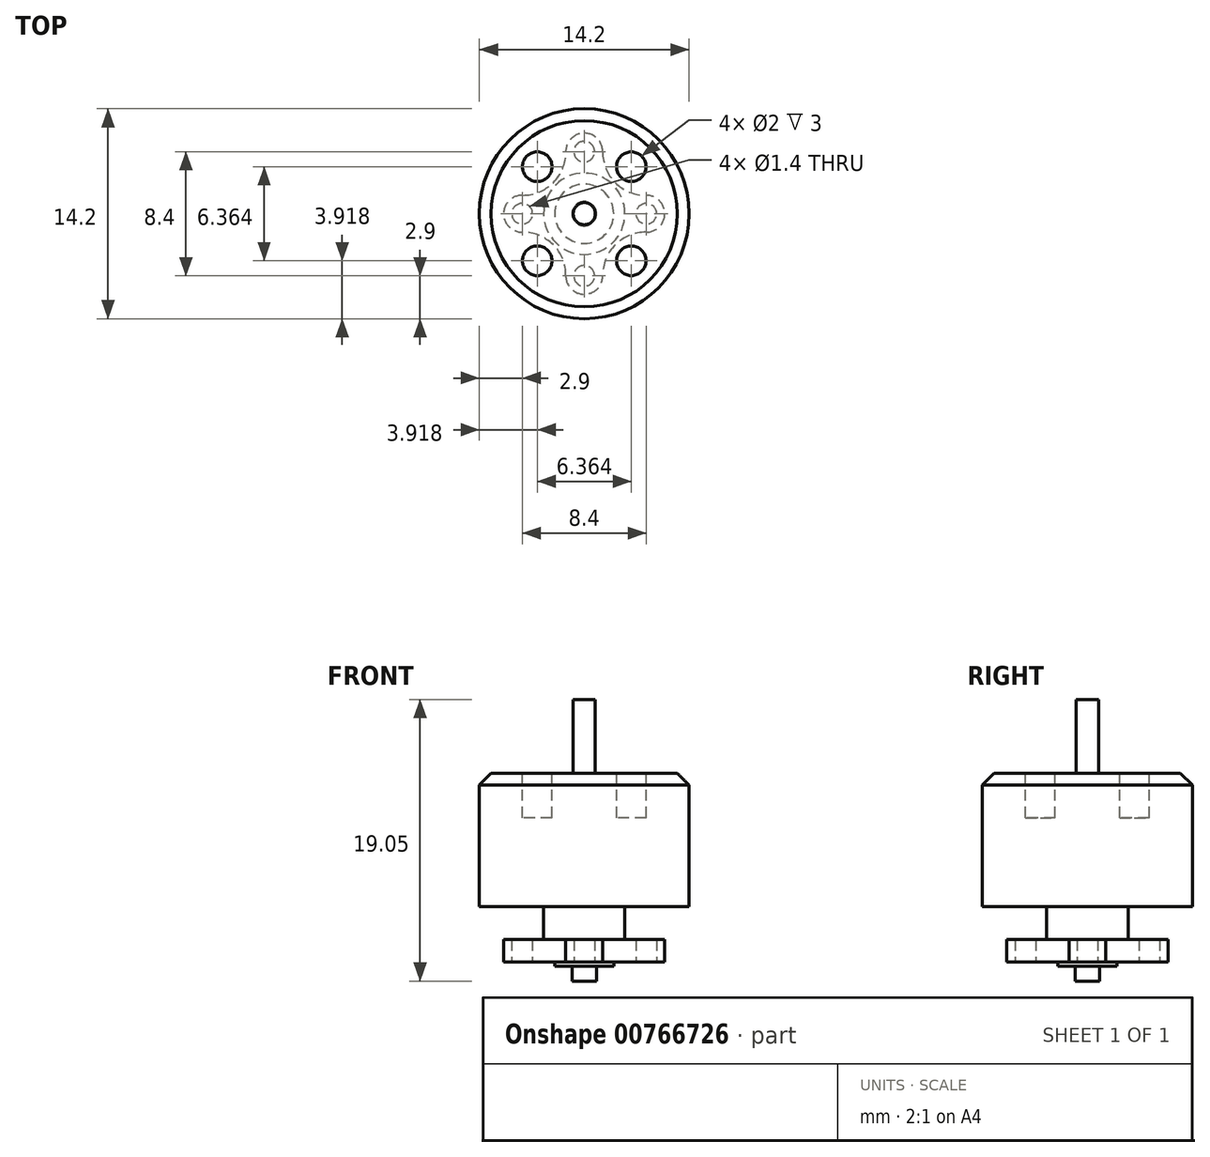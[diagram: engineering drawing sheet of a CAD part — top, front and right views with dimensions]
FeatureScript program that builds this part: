
annotation { "Feature Type Name" : "Feature", "Feature Type Description" : "" }
export const myFeature = defineFeature(function(context is Context, id is Id, definition is map)
    precondition{}
    {
        {
            var Q0;
            Q0=qCreatedBy(makeId("Top.planeOp"),FACE);
            var sketch = newSketch(context, id + "F0", { "sketchPlane" : qUnion([Q0])});
            skCircle(sketch, "E0", {"center": v(0, 0) * mm, "radius": 7.1 * mm});
            skSolve(sketch);
        }
        {
            var Q0;
            Q0 = qSketchRegion(id + "F0", true);
            extrude(context, id + "F1", {"entities" : qUnion([Q0]), "depth" : 9 * mm, "offsetDistance" : 25 * mm});
        }
        {
            var Q0;
            Q0=makeQuery(id+"F1.opExtrude","CAP_FACE",FACE,{"disambiguationData":[OSD([sQuery(id+"F0.wireOp",EDGE,"E0")])],"isStart":false});
            var sketch = newSketch(context, id + "F2", { "sketchPlane" : qUnion([Q0])});
            skCircle(sketch, "E1", {"center": v(0, 0) * mm, "radius": 0.75 * mm});
            skSolve(sketch);
        }
        {
            var Q0;
            Q0 = qSketchRegion(id + "F2", true);
            extrude(context, id + "F3", {"entities" : qUnion([Q0]), "operationType" : NewBodyOperationType.ADD, "depth" : 5 * mm, "offsetDistance" : 25 * mm});
        }
        {
            var Q0;
            Q0=makeQuery(id+"F1.opExtrude","CAP_FACE",FACE,{"disambiguationData":[OSD([sQuery(id+"F0.wireOp",EDGE,"E0")])],"isStart":false});
            var sketch = newSketch(context, id + "F4", { "sketchPlane" : qUnion([Q0])});
            skLineSegment(sketch, "E2.bottom", {"start": v(3.18, 3.18) * mm, "end": v(-3.18, 3.18) * mm, "construction": true});
            skLineSegment(sketch, "E2.top", {"start": v(3.18, -3.18) * mm, "end": v(-3.18, -3.18) * mm, "construction": true});
            skLineSegment(sketch, "E2.left", {"start": v(3.18, 3.18) * mm, "end": v(3.18, -3.18) * mm, "construction": true});
            skLineSegment(sketch, "E2.right", {"start": v(-3.18, 3.18) * mm, "end": v(-3.18, -3.18) * mm, "construction": true});
            skPoint(sketch, "E2.middle", {"position": v(0, 0) * mm});
            skCircle(sketch, "E3", {"center": v(3.18, 3.18) * mm, "radius": 1 * mm});
            skCircle(sketch, "E4", {"center": v(-3.18, 3.18) * mm, "radius": 1 * mm});
            skCircle(sketch, "E5", {"center": v(-3.18, -3.18) * mm, "radius": 1 * mm});
            skCircle(sketch, "E6", {"center": v(3.18, -3.18) * mm, "radius": 1 * mm});
            skSolve(sketch);
        }
        {
            var Q0;
            Q0 = qSketchRegion(id + "F4", true);
            extrude(context, id + "F5", {"entities" : qUnion([Q0]), "operationType" : NewBodyOperationType.REMOVE, "oppositeDirection" : true, "depth" : 3 * mm, "offsetDistance" : 25 * mm});
        }
        {
            var Q0;
            Q0=makeQuery(id+"F1.opExtrude","CAP_FACE",FACE,{"disambiguationData":[OSD([sQuery(id+"F0.wireOp",EDGE,"E0")])],"isStart":true});
            var sketch = newSketch(context, id + "F6", { "sketchPlane" : qUnion([Q0])});
            skCircle(sketch, "E7", {"center": v(0, 0) * mm, "radius": 2.75 * mm});
            skSolve(sketch);
        }
        {
            var Q0;
            Q0 = qSketchRegion(id + "F6", true);
            var Q1;
            Q1=makeQuery(id+"F1.opExtrude","CAP_FACE",FACE,{"disambiguationData":[OSD([sQuery(id+"F0.wireOp",EDGE,"E0")])],"isStart":false});
            extrude(context, id + "F7", {"entities" : qUnion([Q0]), "operationType" : NewBodyOperationType.ADD, "depth" : 3 * mm, "endBoundEntityFace" : qUnion([Q1]), "hasOffset" : true, "offsetDistance" : 12 * mm});
        }
        {
            var Q0;
            Q0=makeQuery(id+"F7.opExtrude","CAP_FACE",FACE,{"disambiguationData":[OSD([sQuery(id+"F6.wireOp",EDGE,"E7")])],"isStart":false});
            var sketch = newSketch(context, id + "F8", { "sketchPlane" : qUnion([Q0])});
            skLineSegment(sketch, "E8", {"start": v(0, 0) * mm, "end": v(4.2, 0) * mm, "construction": true});
            skCircle(sketch, "E9", {"center": v(4.2, 0) * mm, "radius": 0.7 * mm});
            skArc(sketch, "E10", {"start": v(4.19, 1.25) * mm, "mid": v(5.45, 0) * mm, "end": v(4.19, -1.25) * mm});
            skLineSegment(sketch, "E11", {"start": v(0, 0) * mm, "end": v(0, 4.2) * mm, "construction": true});
            skLineSegment(sketch, "E12", {"start": v(0, 4.2) * mm, "end": v(4.2, 0) * mm, "construction": true});
            skArc(sketch, "E13", {"start": v(4.19, 1.25) * mm, "mid": v(3.06, 1.46) * mm, "end": v(2.1, 2.1) * mm});
            skLineSegment(sketch, "E14", {"start": v(0, 1.25) * mm, "end": v(4.19, 1.25) * mm, "construction": true});
            skArc(sketch, "E15.MirrorCS", {"start": v(4.19, -1.25) * mm, "mid": v(3.06, -1.46) * mm, "end": v(2.1, -2.1) * mm});
            skArc(sketch, "E16.1.0", {"start": v(1.25, 4.19) * mm, "mid": v(1.46, 3.06) * mm, "end": v(2.1, 2.1) * mm});
            skArc(sketch, "E16.1.1", {"start": v(-1.25, 4.19) * mm, "mid": v(0, 5.45) * mm, "end": v(1.25, 4.19) * mm});
            skCircle(sketch, "E16.1.2", {"center": v(0, 4.2) * mm, "radius": 0.7 * mm});
            skArc(sketch, "E16.1.3", {"start": v(-1.25, 4.19) * mm, "mid": v(-1.46, 3.06) * mm, "end": v(-2.1, 2.1) * mm});
            skArc(sketch, "E16.2.0", {"start": v(-4.19, 1.25) * mm, "mid": v(-3.06, 1.46) * mm, "end": v(-2.1, 2.1) * mm});
            skArc(sketch, "E16.2.1", {"start": v(-4.19, -1.25) * mm, "mid": v(-5.45, 0) * mm, "end": v(-4.19, 1.25) * mm});
            skCircle(sketch, "E16.2.2", {"center": v(-4.2, 0) * mm, "radius": 0.7 * mm});
            skArc(sketch, "E16.2.3", {"start": v(-4.19, -1.25) * mm, "mid": v(-3.06, -1.46) * mm, "end": v(-2.1, -2.1) * mm});
            skArc(sketch, "E16.3.0", {"start": v(-1.25, -4.19) * mm, "mid": v(-1.46, -3.06) * mm, "end": v(-2.1, -2.1) * mm});
            skArc(sketch, "E16.3.1", {"start": v(1.25, -4.19) * mm, "mid": v(0, -5.45) * mm, "end": v(-1.25, -4.19) * mm});
            skCircle(sketch, "E16.3.2", {"center": v(0, -4.2) * mm, "radius": 0.7 * mm});
            skArc(sketch, "E16.3.3", {"start": v(1.25, -4.19) * mm, "mid": v(1.46, -3.06) * mm, "end": v(2.1, -2.1) * mm});
            skPoint(sketch, "E16.center", {"position": v(0, 0) * mm});
            skSolve(sketch);
        }
        {
            var Q0;
            Q0 = qSketchRegion(id + "F8", true);
            extrude(context, id + "F9", {"entities" : qUnion([Q0]), "operationType" : NewBodyOperationType.ADD, "endBound" : BoundingType.SYMMETRIC, "oppositeDirection" : true, "depth" : 1.5 * mm, "offsetDistance" : 25 * mm});
        }
        {
            var Q0;
            Q0=makeQuery(id+"F9.opExtrude","CAP_FACE",FACE,{"disambiguationData":[OSD([sQuery(id+"F8.wireOp",EDGE,"E9"),sQuery(id+"F8.wireOp",EDGE,"E10"),sQuery(id+"F8.wireOp",EDGE,"E13"),sQuery(id+"F8.wireOp",EDGE,"E15.MirrorCS"),sQuery(id+"F8.wireOp",EDGE,"E16.1.0"),sQuery(id+"F8.wireOp",EDGE,"E16.1.1"),sQuery(id+"F8.wireOp",EDGE,"E16.1.2"),sQuery(id+"F8.wireOp",EDGE,"E16.1.3"),sQuery(id+"F8.wireOp",EDGE,"E16.2.0"),sQuery(id+"F8.wireOp",EDGE,"E16.2.1"),sQuery(id+"F8.wireOp",EDGE,"E16.2.2"),sQuery(id+"F8.wireOp",EDGE,"E16.2.3"),sQuery(id+"F8.wireOp",EDGE,"E16.3.0"),sQuery(id+"F8.wireOp",EDGE,"E16.3.1"),sQuery(id+"F8.wireOp",EDGE,"E16.3.2"),sQuery(id+"F8.wireOp",EDGE,"E16.3.3")])],"isStart":true});
            var sketch = newSketch(context, id + "F10", { "sketchPlane" : qUnion([Q0])});
            skCircle(sketch, "E17", {"center": v(0, 0) * mm, "radius": 2 * mm});
            skSolve(sketch);
        }
        {
            var Q0;
            Q0 = qSketchRegion(id + "F10", true);
            extrude(context, id + "F11", {"entities" : qUnion([Q0]), "operationType" : NewBodyOperationType.ADD, "depth" : 0.3 * mm, "offsetDistance" : 25 * mm});
        }
        {
            var Q0;
            Q0=makeQuery(id+"F11.opExtrude","CAP_FACE",FACE,{"disambiguationData":[OSD([sQuery(id+"F10.wireOp",EDGE,"E17")])],"isStart":false});
            var sketch = newSketch(context, id + "F12", { "sketchPlane" : qUnion([Q0])});
            skCircle(sketch, "E18", {"center": v(0, 0) * mm, "radius": 0.82 * mm});
            skSolve(sketch);
        }
        {
            var Q0;
            Q0 = qSketchRegion(id + "F12", true);
            extrude(context, id + "F13", {"entities" : qUnion([Q0]), "operationType" : NewBodyOperationType.ADD, "depth" : 1 * mm, "offsetDistance" : 25 * mm});
        }
        {
            var Q0;
            Q0=makeQuery(id+"F1.opExtrude","CAP_EDGE",EDGE,{"disambiguationData":[OSD([sQuery(id+"F0.wireOp",EDGE,"E0")])],"isStart":false});
            chamfer(context, id + "F14", {"entities" : qUnion([Q0]), "width" : 0.8 * mm, "tangentPropagation" : true});
        }
    });
